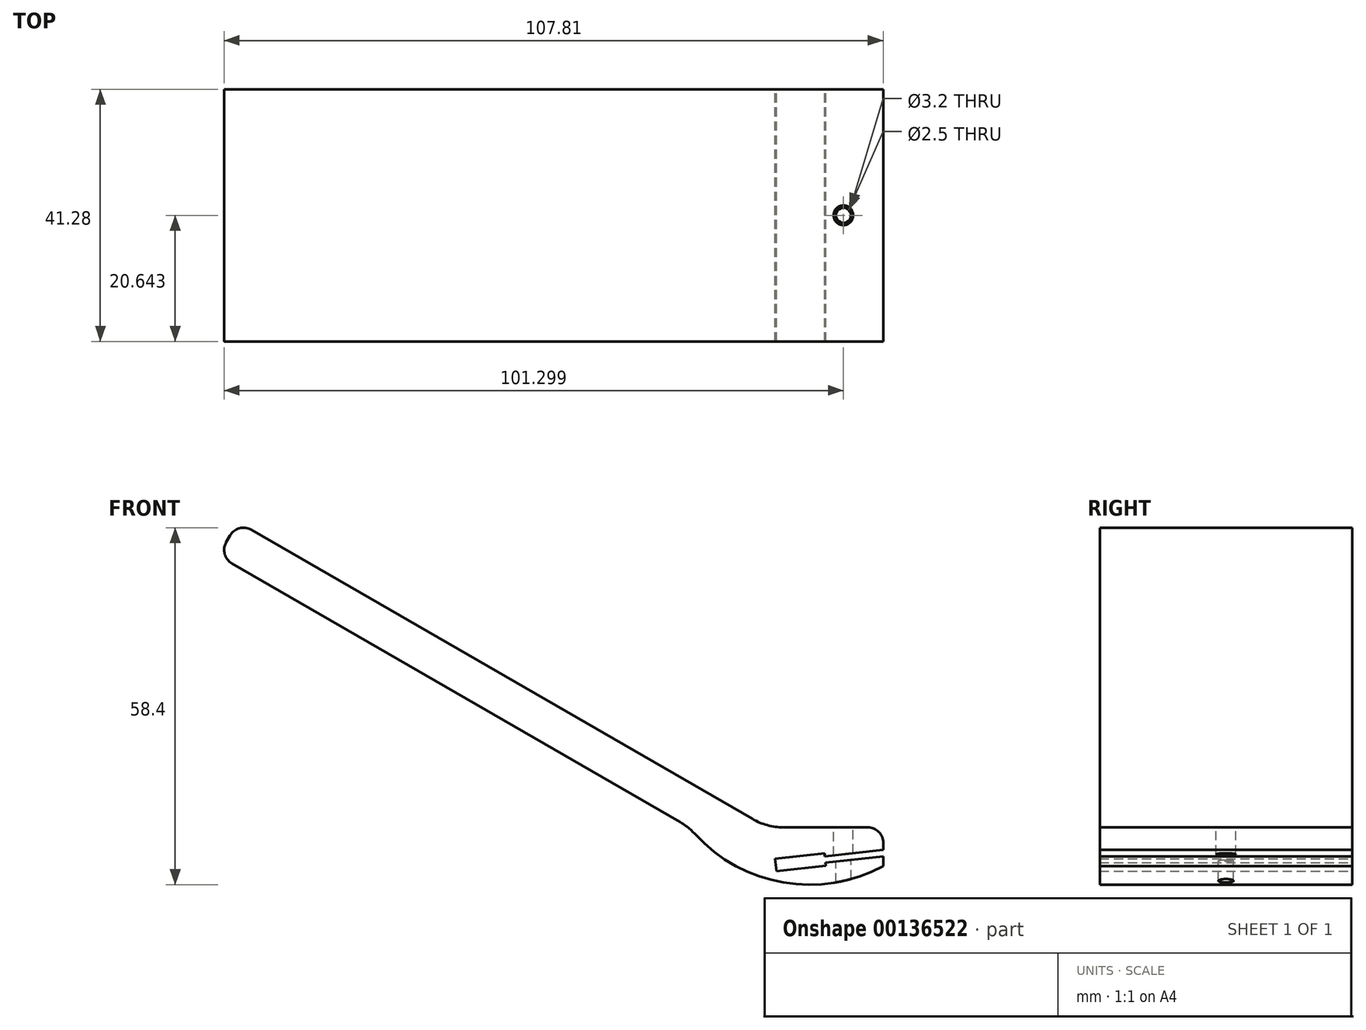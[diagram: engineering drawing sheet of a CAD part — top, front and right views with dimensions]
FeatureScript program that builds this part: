
annotation { "Feature Type Name" : "Feature", "Feature Type Description" : "" }
export const myFeature = defineFeature(function(context is Context, id is Id, definition is map)
    precondition{}
    {
        {
            var Q0;
            Q0=qCreatedBy(makeId("Front.planeOp"),FACE);
            var sketch = newSketch(context, id + "F0", { "sketchPlane" : qUnion([Q0])});
            skLineSegment(sketch, "E0", {"start": v(0, 0) * mm, "end": v(-87.99, 50.8) * mm});
            skLineSegment(sketch, "E1", {"start": v(0, 0) * mm, "end": v(20.75, 0) * mm});
            skLineSegment(sketch, "E2.0", {"start": v(1.7, 6.35) * mm, "end": v(-84.81, 56.3) * mm});
            skLineSegment(sketch, "E2.1", {"start": v(1.7, 6.35) * mm, "end": v(20.75, 6.35) * mm});
            skLineSegment(sketch, "E3", {"start": v(-87.99, 50.8) * mm, "end": v(-84.81, 56.3) * mm});
            skLineSegment(sketch, "E4", {"start": v(20.75, 6.35) * mm, "end": v(20.75, 0) * mm});
            skLineSegment(sketch, "E5.bottom", {"start": v(10.75, 1.03) * mm, "end": v(22.62, 2.33) * mm, "construction": true});
            skLineSegment(sketch, "E5.top", {"start": v(10.75, 1) * mm, "end": v(22.62, 2.3) * mm, "construction": true});
            skLineSegment(sketch, "E5.left", {"start": v(3.68, 0.26) * mm, "end": v(3.68, 0.23) * mm, "construction": true});
            skLineSegment(sketch, "E5.right", {"start": v(22.62, 2.33) * mm, "end": v(22.62, 2.3) * mm, "construction": true});
            skLineSegment(sketch, "E6.bottom", {"start": v(3.63, 0.75) * mm, "end": v(10.7, 1.52) * mm, "construction": true});
            skLineSegment(sketch, "E6.top", {"start": v(3.74, -0.26) * mm, "end": v(10.8, 0.51) * mm, "construction": true});
            skLineSegment(sketch, "E6.left", {"start": v(3.63, 0.75) * mm, "end": v(3.74, -0.26) * mm, "construction": true});
            skLineSegment(sketch, "E6.right", {"start": v(10.7, 1.52) * mm, "end": v(10.75, 1.03) * mm, "construction": true});
            skPoint(sketch, "E7.end.orphan", {"position": v(10.75, 1.02) * mm});
            skPoint(sketch, "E7.start.orphan", {"position": v(3.68, 0.25) * mm});
            skPoint(sketch, "E8.end.orphan", {"position": v(22.62, 2.32) * mm});
            skLineSegment(sketch, "E9.trimOffspring", {"start": v(10.75, 1) * mm, "end": v(10.8, 0.51) * mm, "construction": true});
            skLineSegment(sketch, "E10.0", {"start": v(11.2, 1.6) * mm, "end": v(20.75, 2.64) * mm});
            skLineSegment(sketch, "E10.1", {"start": v(11.15, 2.08) * mm, "end": v(11.2, 1.6) * mm});
            skLineSegment(sketch, "E10.2", {"start": v(3.07, 1.2) * mm, "end": v(11.15, 2.08) * mm});
            skLineSegment(sketch, "E10.3", {"start": v(11.32, 0.56) * mm, "end": v(20.75, 1.59) * mm});
            skLineSegment(sketch, "E10.4", {"start": v(11.32, 0.56) * mm, "end": v(11.37, 0.06) * mm});
            skLineSegment(sketch, "E10.5", {"start": v(3.29, -0.82) * mm, "end": v(11.37, 0.06) * mm});
            skLineSegment(sketch, "E10.6", {"start": v(3.07, 1.2) * mm, "end": v(3.29, -0.82) * mm});
            skArc(sketch, "E11", {"start": v(-11, 6.35) * mm, "mid": v(3.73, -2.54) * mm, "end": v(20.75, 0) * mm});
            skSolve(sketch);
        }
        {
            var Q0;
            Q0=makeQuery(id+"F0.imprint","IMPRINT",FACE,{"disambiguationData":[TD([[makeQuery(id+"F0.imprint","IMPRINT",EDGE,{"derivedFrom":sQuery(id+"F0.wireOp",EDGE,"E0")}),-1.0]])]});
            var Q1;
            {var subQ0=sQuery(id+"F0.wireOp",EDGE,"E1");Q1=makeQuery(id+"F0.imprint","IMPRINT",FACE,{"disambiguationData":[TD([[makeQuery(id+"F0.imprint","IMPRINT",EDGE,{"derivedFrom":subQ0}),-1.0]])]});}
            var Q2;
            {var subQ1=sQuery(id+"F0.wireOp",EDGE,"E10.3");Q2=makeQuery(id+"F0.imprint","IMPRINT",FACE,{"disambiguationData":[TD([[makeQuery(id+"F0.imprint","IMPRINT",EDGE,{"derivedFrom":subQ1}),-1.0]])]});}
            extrude(context, id + "F1", {"entities" : qUnion([Q0, Q1, Q2]), "depth" : 41.27 * mm});
        }
        {
            var Q0;
            Q0=makeQuery(id+"F1.opExtrude","SWEPT_FACE",FACE,{"disambiguationData":[OSD([sQuery(id+"F0.wireOp",EDGE,"E2.1")])]});
            var sketch = newSketch(context, id + "F2", { "sketchPlane" : qUnion([Q0])});
            skLineSegment(sketch, "E12.0.0", {"start": v(11.37, 0) * mm, "end": v(3.29, 0) * mm});
            skLineSegment(sketch, "E12.0.1", {"start": v(3.29, 0) * mm, "end": v(3.29, -41.28) * mm});
            skLineSegment(sketch, "E12.0.2", {"start": v(3.29, -41.28) * mm, "end": v(11.37, -41.28) * mm});
            skLineSegment(sketch, "E12.0.3", {"start": v(11.37, -41.28) * mm, "end": v(11.37, 0) * mm});
            skCircle(sketch, "E13", {"center": v(14.24, -20.64) * mm, "radius": 1.6 * mm});
            skPoint(sketch, "E13.centerSnap0", {"position": v(11.37, -20.64) * mm});
            skCircle(sketch, "E14", {"center": v(14.24, -20.64) * mm, "radius": 1.25 * mm});
            skSolve(sketch);
        }
        {
            var Q0;
            Q0=makeQuery(id+"F2.imprint","IMPRINT",FACE,{"disambiguationData":[TD([[makeQuery(id+"F2.imprint","IMPRINT",EDGE,{"derivedFrom":sQuery(id+"F2.wireOp",EDGE,"E14")}),1.0]])]});
            var Q1;
            Q1=makeQuery(id+"F2.imprint","IMPRINT",FACE,{"disambiguationData":[TD([[makeQuery(id+"F2.imprint","IMPRINT",EDGE,{"derivedFrom":sQuery(id+"F2.wireOp",EDGE,"E13")}),1.0]])]});
            extrude(context, id + "F3", {"entities" : qUnion([Q0, Q1]), "operationType" : NewBodyOperationType.REMOVE, "endBound" : BoundingType.UP_TO_NEXT, "oppositeDirection" : true, "depth" : 25.4 * mm});
        }
        {
            var Q0;
            Q0=makeQuery(id+"F2.imprint","IMPRINT",FACE,{"disambiguationData":[TD([[makeQuery(id+"F2.imprint","IMPRINT",EDGE,{"derivedFrom":sQuery(id+"F2.wireOp",EDGE,"E14")}),1.0]])]});
            extrude(context, id + "F4", {"entities" : qUnion([Q0]), "operationType" : NewBodyOperationType.REMOVE, "endBound" : BoundingType.THROUGH_ALL, "oppositeDirection" : true, "depth" : 25.4 * mm});
        }
        {
            var Q0;
            Q0=makeQuery(id+"F1.opExtrude","SWEPT_FACE",FACE,{"disambiguationData":[OSD([sQuery(id+"F0.wireOp",EDGE,"E2.0")])]});
            var sketch = newSketch(context, id + "F5", { "sketchPlane" : qUnion([Q0])});
            skLineSegment(sketch, "E15", {"start": v(-1.7, -20.64) * mm, "end": v(-101.6, -20.64) * mm, "construction": true});
            skArc(sketch, "E16", {"start": v(-8.05, -41.28) * mm, "mid": v(-48.48, -29.67) * mm, "end": v(-88.9, -41.28) * mm});
            skArc(sketch, "E17.MirrorCS", {"start": v(-8.05, 0) * mm, "mid": v(-48.48, -11.6) * mm, "end": v(-88.9, 0) * mm});
            skSolve(sketch);
        }
        {
            var Q0;
            Q0=makeQuery(id+"F1.opExtrude","SWEPT_EDGE",EDGE,{"disambiguationData":[OSD([sQuery(id+"F0.wireOp",EDGE,"E0"),sQuery(id+"F0.wireOp",EDGE,"E11")])]});
            var Q1;
            {var subQ0=sQuery(id+"F5.wireOp",EDGE,"E16");var subQ1=sQuery(id+"F0.wireOp",EDGE,"E2.0");Q1=makeQuery(id+"FsjUmm3tDMacMcA_1.boolean.opBoolean","COPY",EDGE,{"derivedFrom":makeQuery(id+"FsjUmm3tDMacMcA_1.opExtrude","SWEPT_EDGE",EDGE,{"disambiguationData":[OSD([subQ1,subQ0]),TDD([makeQuery(id+"F5.imprint","INTERSECT",VERTEX,{"disambiguationData":[OD(0.0)],"derivedFrom":[makeQuery(id+"F1.opExtrude","CAP_EDGE",EDGE,{"disambiguationData":[OSD([subQ1])],"isStart":false}),subQ0]})])]})});}
            var Q2;
            Q2=makeQuery(id+"F1.opExtrude","SWEPT_EDGE",EDGE,{"disambiguationData":[OSD([sQuery(id+"F0.wireOp",EDGE,"E2.0"),sQuery(id+"F0.wireOp",EDGE,"E2.1")])]});
            var Q3;
            {var subQ0=sQuery(id+"F5.wireOp",EDGE,"E17.MirrorCS");var subQ1=sQuery(id+"F0.wireOp",EDGE,"E2.0");Q3=makeQuery(id+"FsjUmm3tDMacMcA_1.boolean.opBoolean","COPY",EDGE,{"derivedFrom":makeQuery(id+"FsjUmm3tDMacMcA_1.opExtrude","SWEPT_EDGE",EDGE,{"disambiguationData":[OSD([subQ1,subQ0]),TDD([makeQuery(id+"F5.imprint","INTERSECT",VERTEX,{"disambiguationData":[OD(0.0)],"derivedFrom":[makeQuery(id+"F1.opExtrude","CAP_EDGE",EDGE,{"disambiguationData":[OSD([subQ1])],"isStart":true}),subQ0]})])]})});}
            fillet(context, id + "F6", {"entities" : qUnion([Q0, Q1, Q2, Q3]), "radius" : 10.16 * mm, "tangentPropagation" : true, "allowEdgeOverflow" : false});
        }
        {
            var Q0;
            Q0=makeQuery(id+"F1.opExtrude","SWEPT_EDGE",EDGE,{"disambiguationData":[OSD([sQuery(id+"F0.wireOp",EDGE,"E0"),sQuery(id+"F0.wireOp",EDGE,"E3")])]});
            var Q1;
            Q1=makeQuery(id+"F1.opExtrude","SWEPT_EDGE",EDGE,{"disambiguationData":[OSD([sQuery(id+"F0.wireOp",EDGE,"E2.0"),sQuery(id+"F0.wireOp",EDGE,"E3")])]});
            var Q2;
            Q2=makeQuery(id+"F1.opExtrude","SWEPT_EDGE",EDGE,{"disambiguationData":[OSD([sQuery(id+"F0.wireOp",EDGE,"E2.1"),sQuery(id+"F0.wireOp",EDGE,"E4")])]});
            fillet(context, id + "F7", {"entities" : qUnion([Q0, Q1, Q2]), "radius" : 2.54 * mm, "tangentPropagation" : true, "allowEdgeOverflow" : false});
        }
    });
